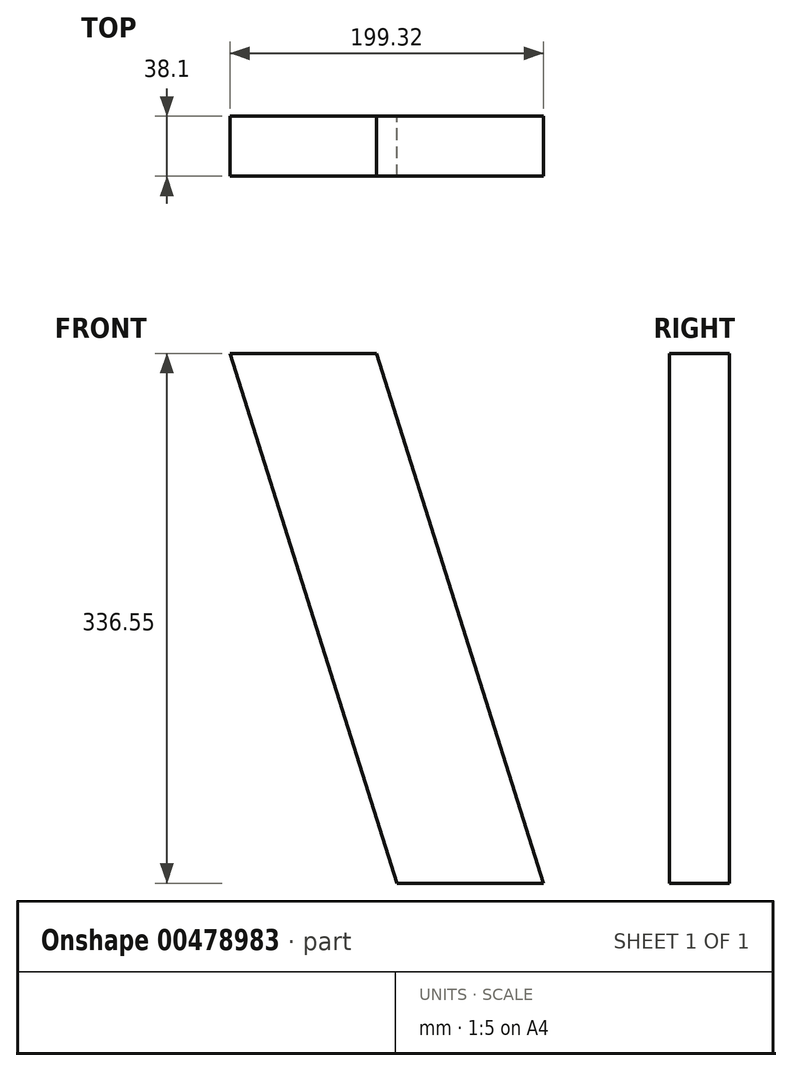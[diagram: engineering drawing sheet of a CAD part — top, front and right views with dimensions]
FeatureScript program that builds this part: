
annotation { "Feature Type Name" : "Feature", "Feature Type Description" : "" }
export const myFeature = defineFeature(function(context is Context, id is Id, definition is map)
    precondition{}
    {
        {
            var Q0;
            Q0=qCreatedBy(makeId("Front.planeOp"),FACE);
            var sketch = newSketch(context, id + "F0", { "sketchPlane" : qUnion([Q0])});
            skLineSegment(sketch, "E0", {"start": v(0, 0) * mm, "end": v(93.21, 0) * mm});
            skLineSegment(sketch, "E1", {"start": v(93.21, 0) * mm, "end": v(-12.9, 336.55) * mm});
            skLineSegment(sketch, "E2", {"start": v(-12.9, 336.55) * mm, "end": v(-106.11, 336.55) * mm});
            skLineSegment(sketch, "E3", {"start": v(-106.11, 336.55) * mm, "end": v(0, 0) * mm});
            skSolve(sketch);
        }
        {
            var Q0;
            Q0 = qSketchRegion(id + "F0", true);
            extrude(context, id + "F1", {"entities" : qUnion([Q0]), "depth" : 38.1 * mm});
        }
    });
